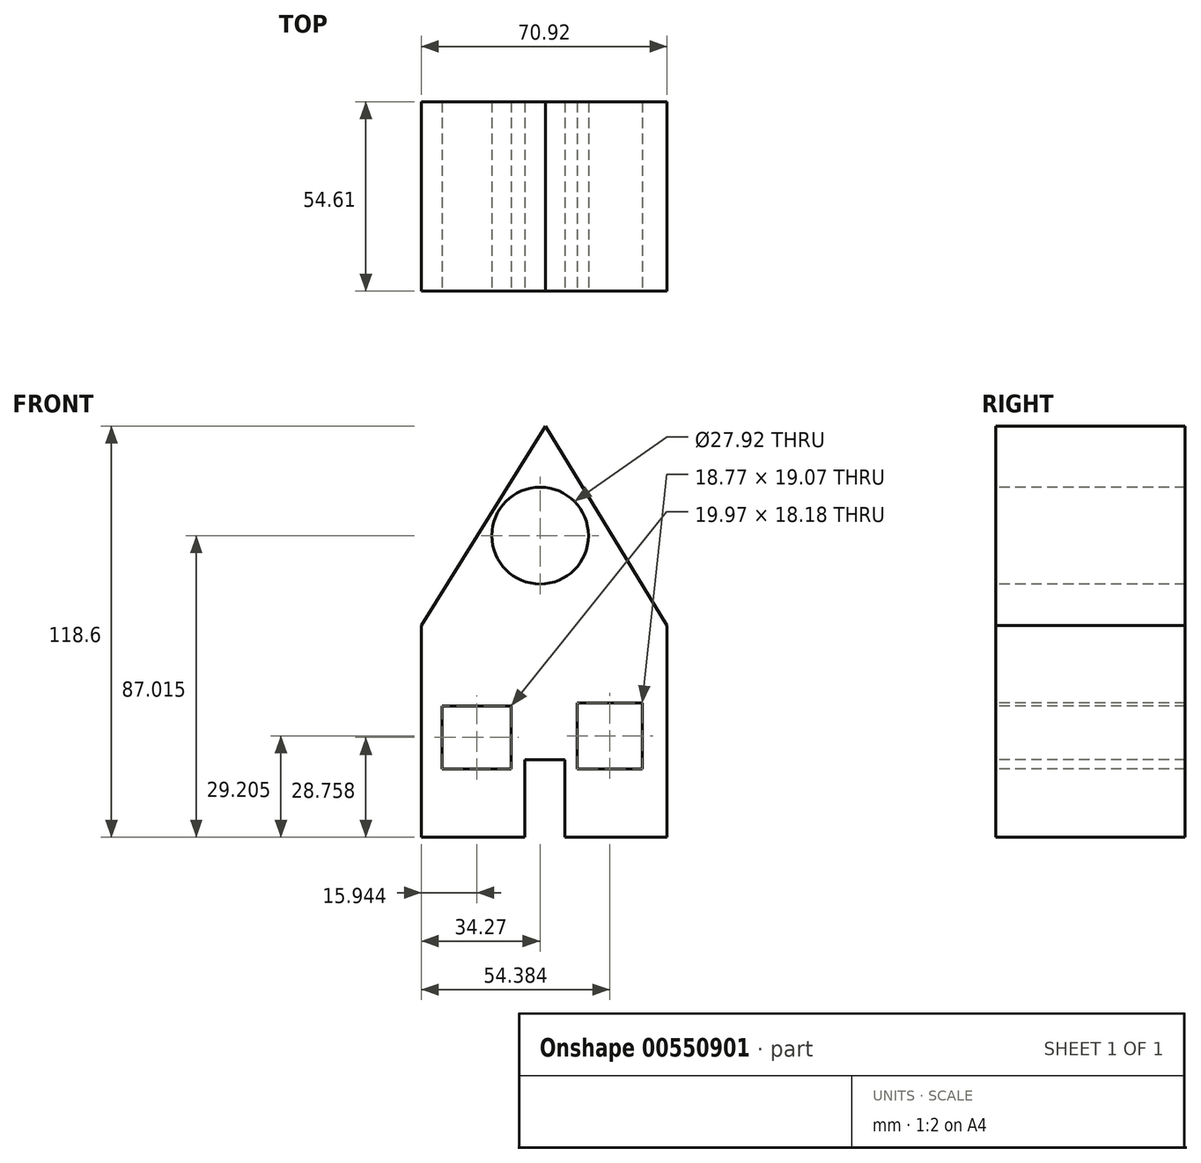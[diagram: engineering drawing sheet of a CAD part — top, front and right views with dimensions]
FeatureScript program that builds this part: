
annotation { "Feature Type Name" : "Feature", "Feature Type Description" : "" }
export const myFeature = defineFeature(function(context is Context, id is Id, definition is map)
    precondition{}
    {
        {
            var Q0;
            Q0=qCreatedBy(makeId("Front.planeOp"),FACE);
            var sketch = newSketch(context, id + "F0", { "sketchPlane" : qUnion([Q0])});
            skLineSegment(sketch, "E0.bottom", {"start": v(-29.8, -14.75) * mm, "end": v(41.12, -14.75) * mm});
            skLineSegment(sketch, "E0.top", {"start": v(-29.8, -75.84) * mm, "end": v(41.12, -75.84) * mm});
            skLineSegment(sketch, "E0.left", {"start": v(-29.8, -14.75) * mm, "end": v(-29.8, -75.84) * mm});
            skLineSegment(sketch, "E0.right", {"start": v(41.12, -14.75) * mm, "end": v(41.12, -75.84) * mm});
            skLineSegment(sketch, "E1", {"start": v(-29.8, -14.75) * mm, "end": v(5.96, 42.76) * mm});
            skLineSegment(sketch, "E2", {"start": v(5.96, 42.76) * mm, "end": v(41.12, -14.75) * mm});
            skLineSegment(sketch, "E3.bottom", {"start": v(-23.84, -38) * mm, "end": v(-3.87, -38) * mm});
            skLineSegment(sketch, "E3.top", {"start": v(-23.84, -56.17) * mm, "end": v(-3.87, -56.17) * mm});
            skLineSegment(sketch, "E3.left", {"start": v(-23.84, -38) * mm, "end": v(-23.84, -56.17) * mm});
            skLineSegment(sketch, "E3.right", {"start": v(-3.87, -38) * mm, "end": v(-3.87, -56.17) * mm});
            skLineSegment(sketch, "E4.bottom", {"start": v(33.97, -37.1) * mm, "end": v(15.2, -37.1) * mm});
            skLineSegment(sketch, "E4.top", {"start": v(33.97, -56.17) * mm, "end": v(15.2, -56.17) * mm});
            skLineSegment(sketch, "E4.left", {"start": v(33.97, -37.1) * mm, "end": v(33.97, -56.17) * mm});
            skLineSegment(sketch, "E4.right", {"start": v(15.2, -37.1) * mm, "end": v(15.2, -56.17) * mm});
            skLineSegment(sketch, "E5.bottom", {"start": v(0, -53.49) * mm, "end": v(11.62, -53.49) * mm});
            skLineSegment(sketch, "E5.top", {"start": v(0, -75.84) * mm, "end": v(11.62, -75.84) * mm});
            skLineSegment(sketch, "E5.left", {"start": v(0, -53.49) * mm, "end": v(0, -75.84) * mm});
            skLineSegment(sketch, "E5.right", {"start": v(11.62, -53.49) * mm, "end": v(11.62, -75.84) * mm});
            skLineSegment(sketch, "E6", {"start": v(-13.86, -38) * mm, "end": v(-13.86, -56.17) * mm});
            skLineSegment(sketch, "E7", {"start": v(-23.84, -47.08) * mm, "end": v(-3.87, -47.08) * mm});
            skLineSegment(sketch, "E8", {"start": v(24.58, -37.1) * mm, "end": v(24.58, -56.17) * mm});
            skLineSegment(sketch, "E9", {"start": v(15.2, -46.64) * mm, "end": v(33.97, -46.64) * mm});
            skCircle(sketch, "E10", {"center": v(4.47, 11.17) * mm, "radius": 13.96 * mm});
            skLineSegment(sketch, "E11", {"start": v(4.14, 25.13) * mm, "end": v(4.47, -2.78) * mm});
            skLineSegment(sketch, "E12", {"start": v(-9.48, 10.88) * mm, "end": v(18.43, 11.21) * mm});
            skSolve(sketch);
        }
        {
            var Q0;
            Q0=makeQuery(id+"F0.imprint","IMPRINT",FACE,{"disambiguationData":[TD([[makeQuery(id+"F0.imprint","IMPRINT",EDGE,{"derivedFrom":sQuery(id+"F0.wireOp",EDGE,"E0.bottom")}),1.0]])]});
            var Q1;
            Q1=makeQuery(id+"F0.imprint","IMPRINT",FACE,{"disambiguationData":[TD([[makeQuery(id+"F0.imprint","IMPRINT",EDGE,{"derivedFrom":sQuery(id+"F0.wireOp",EDGE,"E0.bottom")}),-1.0]])]});
            extrude(context, id + "F1", {"entities" : qUnion([Q0, Q1]), "oppositeDirection" : true, "depth" : 54.6 * mm, "offsetDistance" : 25.4 * mm});
        }
    });
